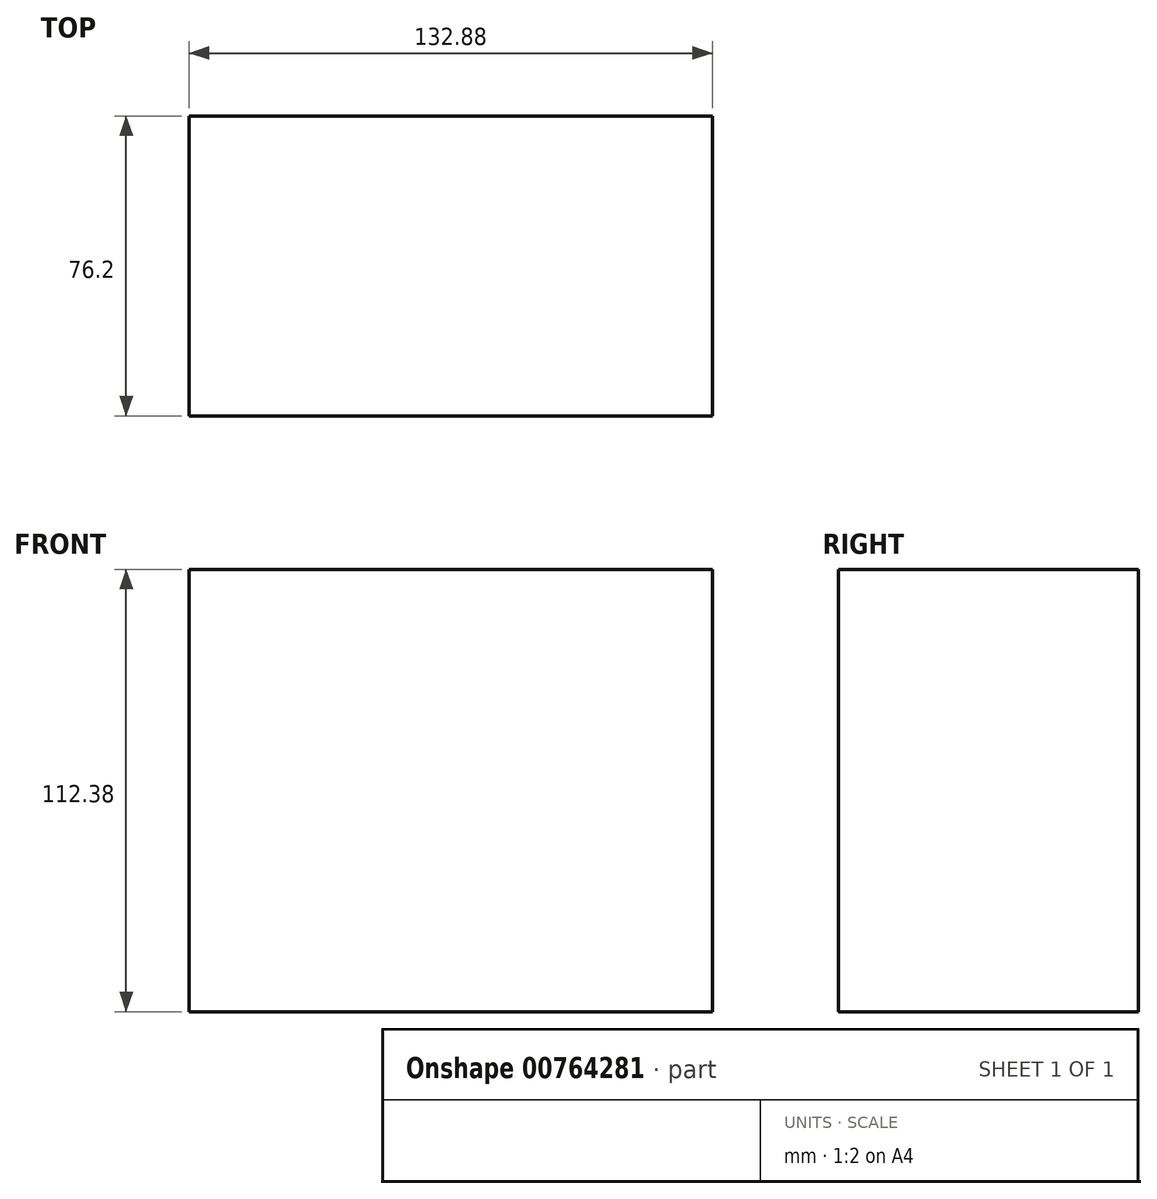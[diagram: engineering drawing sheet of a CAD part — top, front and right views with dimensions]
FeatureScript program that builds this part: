
annotation { "Feature Type Name" : "Feature", "Feature Type Description" : "" }
export const myFeature = defineFeature(function(context is Context, id is Id, definition is map)
    precondition{}
    {
        {
            var Q0;
            Q0=qCreatedBy(makeId("Front.planeOp"),FACE);
            var sketch = newSketch(context, id + "F0", { "sketchPlane" : qUnion([Q0])});
            skLineSegment(sketch, "E0.bottom", {"start": v(-66.44, 56.19) * mm, "end": v(66.44, 56.19) * mm});
            skLineSegment(sketch, "E0.top", {"start": v(-66.44, -56.19) * mm, "end": v(66.44, -56.19) * mm});
            skLineSegment(sketch, "E0.left", {"start": v(-66.44, 56.19) * mm, "end": v(-66.44, -56.19) * mm});
            skLineSegment(sketch, "E0.right", {"start": v(66.44, 56.19) * mm, "end": v(66.44, -56.19) * mm});
            skPoint(sketch, "E0.middle", {"position": v(0, 0) * mm});
            skSolve(sketch);
        }
        {
            var Q0;
            Q0=makeQuery(id+"F0.imprint","IMPRINT",FACE,{"disambiguationData":[TD([[makeQuery(id+"F0.imprint","IMPRINT",EDGE,{"derivedFrom":sQuery(id+"F0.wireOp",EDGE,"E0.bottom")}),-1.0]])]});
            extrude(context, id + "F1", {"entities" : qUnion([Q0]), "depth" : 76.2 * mm, "offsetDistance" : 25.4 * mm});
        }
    });
